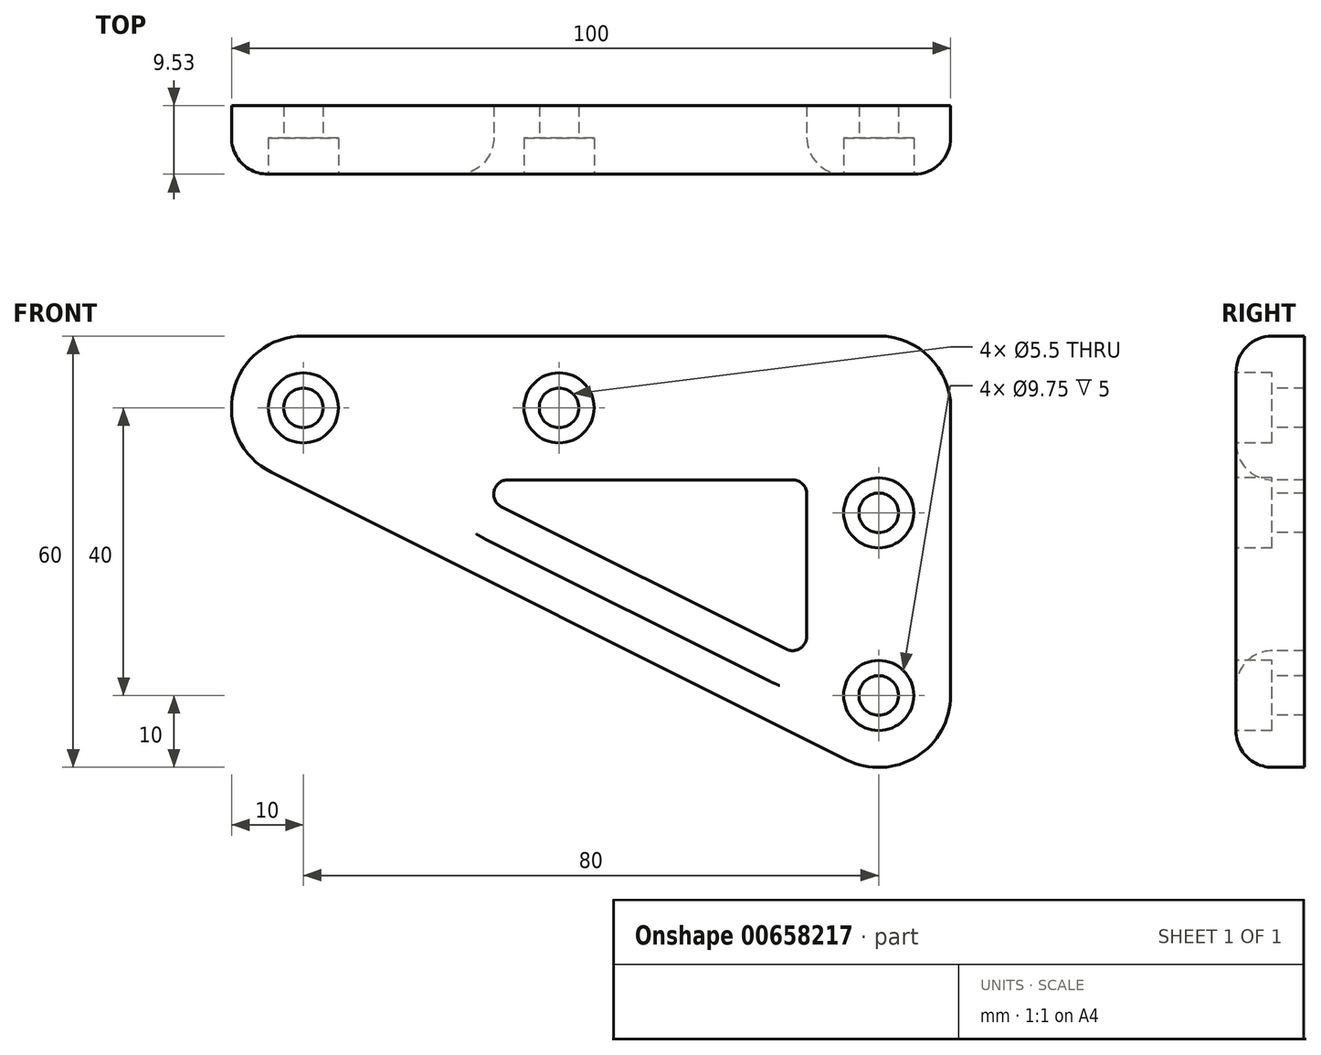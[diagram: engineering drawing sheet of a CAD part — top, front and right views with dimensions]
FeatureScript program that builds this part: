
annotation { "Feature Type Name" : "Feature", "Feature Type Description" : "" }
export const myFeature = defineFeature(function(context is Context, id is Id, definition is map)
    precondition{}
    {
        {
            var Q0;
            Q0=qCreatedBy(makeId("Front.planeOp"),FACE);
            var sketch = newSketch(context, id + "F0", { "sketchPlane" : qUnion([Q0])});
            skPoint(sketch, "E0.MirrorP", {"position": v(-44.45, 0) * mm});
            skArc(sketch, "E1", {"start": v(10, 0) * mm, "mid": v(7.07, 7.07) * mm, "end": v(0, 10) * mm});
            skPoint(sketch, "E2", {"position": v(0, -40) * mm});
            skArc(sketch, "E3", {"start": v(-4.47, -48.94) * mm, "mid": v(5.26, -48.5) * mm, "end": v(10, -40) * mm});
            skArc(sketch, "E4", {"start": v(-80, 10) * mm, "mid": v(-89.73, 2.3) * mm, "end": v(-84.47, -8.94) * mm});
            skLineSegment(sketch, "E5", {"start": v(-84.47, -8.94) * mm, "end": v(-4.47, -48.94) * mm});
            skLineSegment(sketch, "E6", {"start": v(-80, 10) * mm, "end": v(0, 10) * mm});
            skLineSegment(sketch, "E7", {"start": v(10, -40) * mm, "end": v(10, 0) * mm});
            skLineSegment(sketch, "E8.0", {"start": v(-52.42, -13.79) * mm, "end": v(-12.9, -33.55) * mm});
            skLineSegment(sketch, "E9.0", {"start": v(-10, -31.76) * mm, "end": v(-10, -12) * mm});
            skLineSegment(sketch, "E10.0", {"start": v(-51.53, -10) * mm, "end": v(-12, -10) * mm});
            skPoint(sketch, "E11.visualSharp", {"position": v(-60, -10) * mm});
            skArc(sketch, "E11.filletArc", {"start": v(-51.53, -10) * mm, "mid": v(-53.47, -11.54) * mm, "end": v(-52.42, -13.79) * mm});
            skPoint(sketch, "E12.visualSharp", {"position": v(-10, -10) * mm});
            skArc(sketch, "E12.filletArc", {"start": v(-10, -12) * mm, "mid": v(-10.59, -10.59) * mm, "end": v(-12, -10) * mm});
            skPoint(sketch, "E13.visualSharp", {"position": v(-10, -35) * mm});
            skArc(sketch, "E13.filletArc", {"start": v(-12.9, -33.55) * mm, "mid": v(-10.95, -33.47) * mm, "end": v(-10, -31.76) * mm});
            skPoint(sketch, "E14", {"position": v(0, -14.6) * mm});
            skSolve(sketch);
        }
        {
            var Q0;
            Q0 = qSketchRegion(id + "F0", true);
            extrude(context, id + "F1", {"entities" : qUnion([Q0]), "oppositeDirection" : true, "depth" : 9.52 * mm, "offsetDistance" : 25.4 * mm});
        }
        {
            var Q0;
            Q0=sQuery(id+"F0.wireOp",VERTEX,"E2");
            var Q1;
            Q1=sQuery(id+"F0.wireOp",VERTEX,"E0.MirrorP");
            var Q2;
            Q2=sQuery(id+"F0.wireOp",VERTEX,"E4.center");
            var Q3;
            Q3=sQuery(id+"F0.wireOp",VERTEX,"E14");
            var Q4;
            Q4=makeQuery(id+"F1.opExtrude","SWEPT_BODY",BODY,{"disambiguationData":[OSD([sQuery(id+"F0.wireOp",EDGE,"bf2f238d-4e1d-4e86-ab75-1465cd813df2.MirrorCS"),sQuery(id+"F0.wireOp",EDGE,"7d5bedbb-471c-4160-8e68-eb1f4d767648.MirrorCS"),sQuery(id+"F0.wireOp",EDGE,"bc7fee83-9e46-4c51-805a-8ae9689402aa.MirrorCS"),sQuery(id+"F0.wireOp",EDGE,"e5d497b7-cccf-4703-a1dc-18e520bbeae9.MirrorCS"),sQuery(id+"F0.wireOp",EDGE,"c155fd9a-5cc5-4759-a1c6-071fd15af197.MirrorCS"),sQuery(id+"F0.wireOp",EDGE,"33a989d6-5cc4-4172-ab73-ca817da9f412.MirrorCS"),sQuery(id+"F0.wireOp",EDGE,"1c3aec17-fec7-453e-8acd-3df81b9bc4e3.MirrorCS"),sQuery(id+"F0.wireOp",EDGE,"0cd19f4d-6d86-4b4a-a093-bb589b475590.MirrorCS"),sQuery(id+"F0.wireOp",EDGE,"eee5d6f5-912f-4719-99ba-1d72e724f1e9.MirrorCS"),sQuery(id+"F0.wireOp",EDGE,"64a401ff-d109-42b1-96b9-6f7f2e519c4d.MirrorCS"),sQuery(id+"F0.wireOp",EDGE,"2bc110f3-ae92-45de-b2b7-7df43831b8ab"),sQuery(id+"F0.wireOp",EDGE,"pibmvETk-c1Xj-BIgN-8uma-1jo4IxxjolSW")])]});
            var Q5;
            Q5=makeQuery(id+"F1.opExtrude","SWEPT_BODY",BODY,{"disambiguationData":[OSD([sQuery(id+"F0.wireOp",EDGE,"E1"),sQuery(id+"F0.wireOp",EDGE,"E3"),sQuery(id+"F0.wireOp",EDGE,"E4"),sQuery(id+"F0.wireOp",EDGE,"E5"),sQuery(id+"F0.wireOp",EDGE,"E6"),sQuery(id+"F0.wireOp",EDGE,"E7"),sQuery(id+"F0.wireOp",EDGE,"E8.0"),sQuery(id+"F0.wireOp",EDGE,"E9.0"),sQuery(id+"F0.wireOp",EDGE,"E10.0"),sQuery(id+"F0.wireOp",EDGE,"E11.filletArc"),sQuery(id+"F0.wireOp",EDGE,"E12.filletArc"),sQuery(id+"F0.wireOp",EDGE,"E13.filletArc")])]});
            hole(context, id + "F2", {"style" : HoleStyle.C_BORE, "endStyle" : HoleEndStyle.THROUGH, "standardTappedOrClearance" : lookupTablePath({ "standard" : "ISO", "fit" : "Normal", "size" : "M5", "type" : "Clearance" }), "standardBlindInLast" : lookupTablePath({ "fit" : "Standard", "standard" : "ISO", "size" : "M5", "type" : "Clearance" }), "holeDiameter" : 5.5 * mm, "cBoreDiameter" : 9.75 * mm, "cBoreDepth" : 5 * mm, "majorDiameter" : 6.35 * mm, "isTappedThrough" : true, "tappedDepth" : 12.7 * mm, "tapClearance" : 3, "locations" : qUnion([Q0, Q1, Q2, Q3]), "scope" : qUnion([Q4, Q5])});
        }
        {
            var Q0;
            Q0=makeQuery(id+"F1.opExtrude","CAP_EDGE",EDGE,{"disambiguationData":[OSD([sQuery(id+"F0.wireOp",EDGE,"E6")])],"isStart":true});
            var Q1;
            Q1=makeQuery(id+"F1.opExtrude","CAP_EDGE",EDGE,{"disambiguationData":[OSD([sQuery(id+"F0.wireOp",EDGE,"E10.0")])],"isStart":true});
            fillet(context, id + "F3", {"entities" : qUnion([Q0, Q1]), "radius" : 5.08 * mm, "tangentPropagation" : true, "allowEdgeOverflow" : false});
        }
    });
